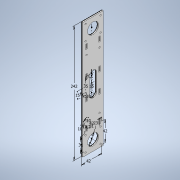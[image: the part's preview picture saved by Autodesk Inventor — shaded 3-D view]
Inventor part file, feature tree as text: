
AUTODESK INVENTOR PART (.ipt)
format: ipt  version: 2021 (Build 250183000, 183)  size: 182,784 bytes
history: native  units: mm
features: other x1, sketch x1, extrude x1, hole x1, mirror x1
ambient origin geometry x8: Origin, YZ Plane, XZ Plane, XY Plane, X Axis, Y Axis, Z Axis, Center Point
bodies: Body1 (feature_tree)
feature tree (5):
  other  "Sólido1"
  sketch  "Esboço1"  dims[d0=242.0mm d1=42.0mm d2=42.0mm d3=42.0mm d4=31.0mm d5=31.0mm d6=23.0mm d7=15.0mm d8=35.0mm d9=10.2mm d10=3.0mm d12=6.0mm d13=10.2mm d14=3.0mm d15=15.0mm d16=10.0mm d17=10.0mm d18=3.0mm d19=0.0mm d20=3.0mm d21=6.0mm d22=4.0mm d23=2.0mm d24=90.0deg d25=8.0mm d26=20.594885mm]
  extrude  "Extrusão1"  Depth=42.0mm
  hole  "Furo1"  [1 undecoded]
  mirror  "Espelhamento1"
note: 1 required parameter value undecoded (feature->parameter linkage not recoverable at this tier; creation-order binding heuristic only, values carry confidence <= 0.55)
